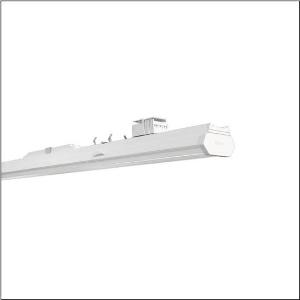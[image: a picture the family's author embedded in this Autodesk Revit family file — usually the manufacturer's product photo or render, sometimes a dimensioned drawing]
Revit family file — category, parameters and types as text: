
# Revit family: licross_21_protected_ho_52td11mn4fxs
name_source: partatom
category: Lighting Fixtures
units: mm (PartAtom-declared; Revit-internal decimal feet)

## family parameters
Cut with Voids When Loaded = No
Host = Face
Light Source = No
Part Type = Normal
Room Calculation Point = No
Round Connector Dimension = Use Diameter
Shared = No

## types (1)
- --- (1 x LED, 15020 lm, 83.2 W, 4000K)
    Apparent Load = 83 VA
    CIE Flux Codes = 84 94 98 99 100
    Color Rendering = 80
    Color Temperature = 4000K
    Default Elevation = 1800 mm
    Description = Licross 21 Protected HO, luminaire insert, of sheet steel, galvanised, coil coated, white, length: 1.500mm, width: 66mm, height: 67mm, LED rated luminous flux: 15.020lm, light colour: 840, SDCM (Standard Deviation of Colour Matching)MacAdam ≤ 3 SDCM (initial), control gear: ON/OFF Multilumen, with plug, 3-pole, with phase selection, mains connection: 220..240V, AC, 50/60Hz, rated input power: 83W, internal wiring halogen-free, primary light control with lens, of plastic, primary optical cover: cover, of PMMA, light emission: direct distribution, primary light characteristic: symmetric, protection rating (complete): IP54, insulation class (complete): insulation class I (protective earthing), certification: CE, ENEC, VDE, UKCA, protection symbol: D if used in an environment with non-conductive dust loads with corresponding accessories, impact resistance: IK06, permissible ambient temperature for indoor applications: -35..+35°C, corresponds to IFS (International Featured Standards) requirements for safety and quality in the food industry, reducing of maximum allowable ambient temperature of 5°C with ceiling mounting, LABS conformity tested according to VDMA 24364:2018-05, The light source and the operating device comply with the requirements of the Ecodesign Regulation (EU) 2019/2020 and are replaceable in accordance with this regulation, packaging unit: 1 piece
    Height = 92 mm
    Lamp = 1 x LED
    Lamp Light Flux = 15020 lm
    Lamp Power = 83.2 W
    Lamp count = 1
    Length = 1500 mm
    Luminous efficacy = 181 lm/W
    Manufacturer = Siteco
    ModVariant = No
    Model = 52TD11MN4FXS
    Mounting Place = Ceiling
    Mounting Type = Pendant
    Number of Poles = 1
    OnlyDefault = Yes
    Power Factor = 1
    Product Name = Licross 21 Protected HO
    Product group = luminaire insert | ceiling pendant
    ProductGroupID = 901
    Protection Class = Protection class I
    Protection Degree = IP 54
    RLX_Detail_Level = 1
    RLX_Emergency_Light_Flux = 0 lm
    RLX_Emergency_Type = 0
    RLX_Emergency_Type_DB = No
    RlxData = <blob elided: 22237 chars, md5=6f48b91a>
    Socket = socket
    Standby Power = 0 W
    System Light Flux = 15020 lm
    System Power = 83 W
    Type Comments = factory setting: luminous flux: 100 % | (A | C | E) | 195 mA
    Type Image = l_1256148.jpg
    URL = http://relux.com
    VarID = @adj_110611
    Voltage = 0 V
    Weight = 0.00 kg
    Width = 88 mm

## geometry (parser evidence)
native form markers: Blend x4, Sweep x10
no freeform markers — native parametric forms only
